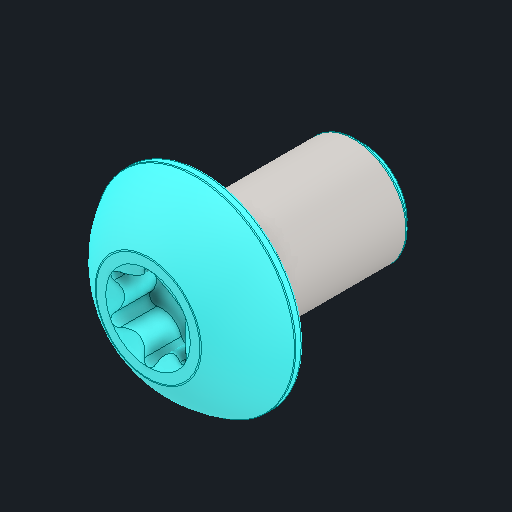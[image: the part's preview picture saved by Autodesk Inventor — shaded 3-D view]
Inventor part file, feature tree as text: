
AUTODESK INVENTOR PART (.ipt)
format: ipt  version: 2025 (Build 290162000, 162)  size: 189,952 bytes
history: native  units: in
note: dims shown in document units (in); Inventor stores cm internally (conversion verified against a paired STEP export)
features: fillet x1
ambient origin geometry x8: Origin, YZ Plane, XZ Plane, XY Plane, X Axis, Y Axis, Z Axis, Center Point
bodies: Solid1 (feature_tree)
feature tree (1):
  fillet  "Fillet1"  [1 undecoded]
note: 1 required parameter value undecoded (feature->parameter linkage not recoverable at this tier; creation-order binding heuristic only, values carry confidence <= 0.55)
